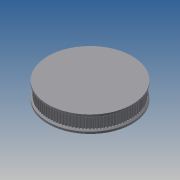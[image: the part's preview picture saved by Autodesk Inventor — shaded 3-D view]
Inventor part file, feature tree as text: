
AUTODESK INVENTOR PART (.ipt)
format: ipt  version: 2013 (Build 170138000, 138)  size: 1,192,448 bytes
history: native  units: mm
features: extrude x5, sketch x5, pattern_circular x1, chamfer x1, mirror x1
ambient origin geometry x8: Origin, YZ Plane, XZ Plane, XY Plane, X Axis, Y Axis, Z Axis, Center Point
bodies: Solid1 (feature_tree)
feature tree (13):
  extrude  "Extrusion1"  Depth=0.628319mm
  pattern_circular  "Circular Pattern1"  [2 undecoded]
  extrude  "Extrusion3"  Depth=0.75mm
  chamfer  "Chamfer2"  Distance=0.254mm
  mirror  "Mirror1"
  extrude  "Extrusion4"  Depth=8.0mm TaperAngle=0.0deg
  extrude  "Extrusion5"  Depth=1000.0mm
  extrude  "Extrusion6"  TaperAngle=360.0deg  [1 undecoded]
  sketch  "Sketch1"  dims[d0=63.661977mm d9=0.628319mm]
  sketch  "Sketch3"  dims[d11=0.254mm]
  sketch  "Sketch4"  dims[d12=0.3mm]
  sketch  "Sketch5"  dims[d13=0.4mm]
  sketch  "Sketch6"  dims[d14=1.0mm d15=0.555mm d16=0.75mm d17=0.254mm d18=8.0mm d19=0.0mm d20=1000.0mm d21=360.0deg d23=0.1mm d32=2.5mm d33=0.0mm d34=1.0mm d35=2.0mm d36=45.0deg d37=15.0mm d39=3.5mm d40=15.0mm d41=25.0mm d42=2.0mm d43=0.0mm d44=6.0mm d46=3.0mm d47=0.0mm d49=22.0mm d51=7.0mm d52=0.0mm d53=1.0mm]
note: 3 required parameter values undecoded (feature->parameter linkage not recoverable at this tier; creation-order binding heuristic only, values carry confidence <= 0.55)
